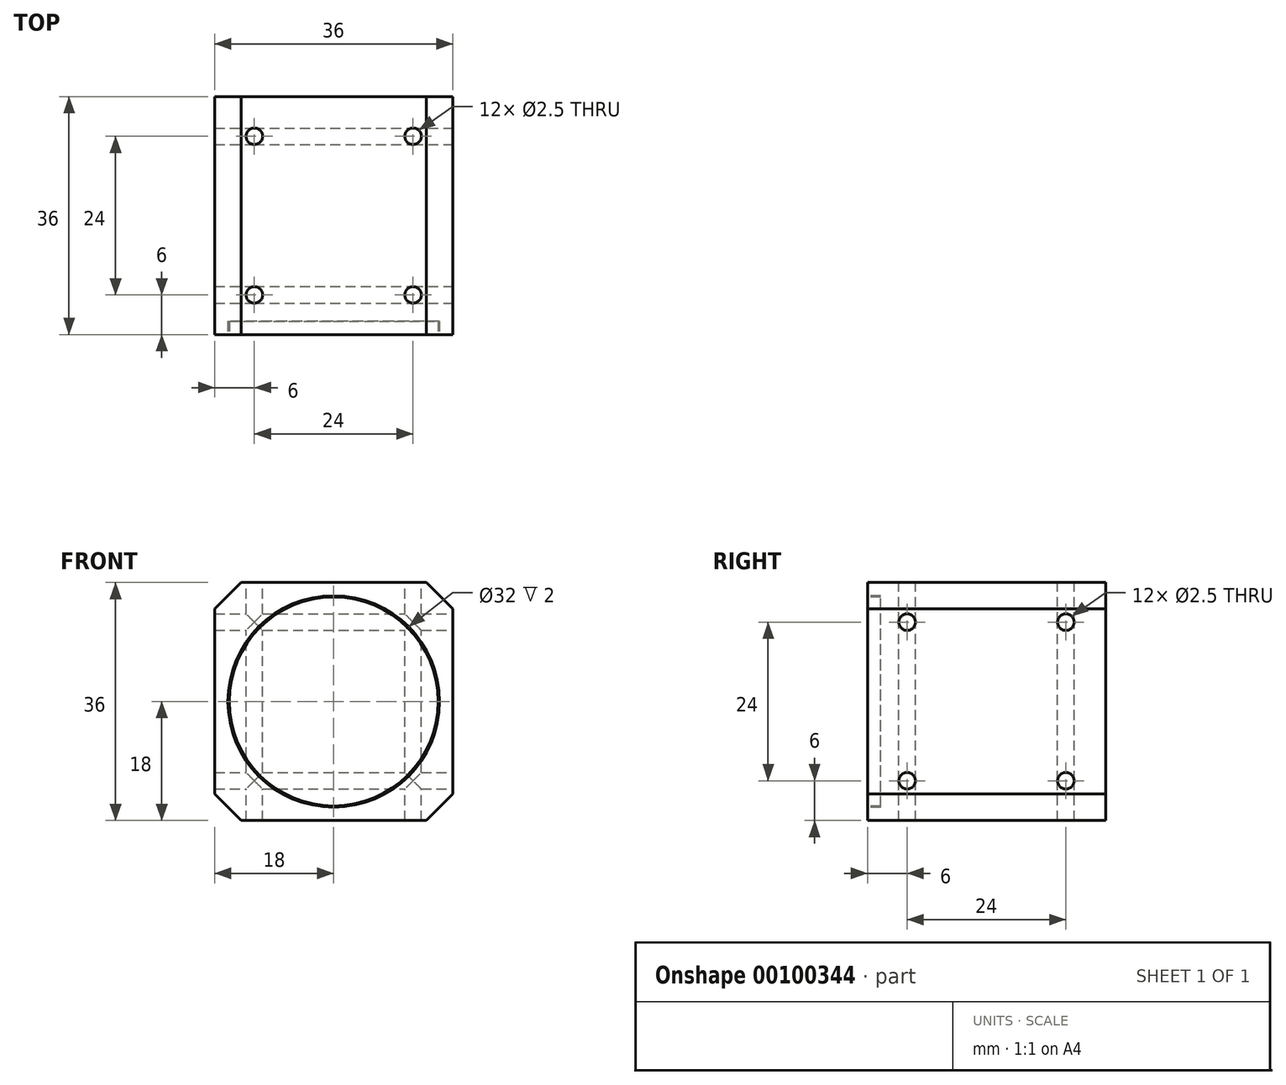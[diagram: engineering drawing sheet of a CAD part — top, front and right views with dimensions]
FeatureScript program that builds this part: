
annotation { "Feature Type Name" : "Feature", "Feature Type Description" : "" }
export const myFeature = defineFeature(function(context is Context, id is Id, definition is map)
    precondition{}
    {
        {
            var Q0;
            Q0=qCreatedBy(makeId("Front.planeOp"),FACE);
            var sketch = newSketch(context, id + "F0", { "sketchPlane" : qUnion([Q0])});
            skLineSegment(sketch, "E0.bottom", {"start": v(18, -18) * mm, "end": v(-18, -18) * mm});
            skLineSegment(sketch, "E0.top", {"start": v(18, 18) * mm, "end": v(-18, 18) * mm});
            skLineSegment(sketch, "E0.left", {"start": v(18, -18) * mm, "end": v(18, 18) * mm});
            skLineSegment(sketch, "E0.right", {"start": v(-18, -18) * mm, "end": v(-18, 18) * mm});
            skPoint(sketch, "E0.middle", {"position": v(0, 0) * mm});
            skSolve(sketch);
        }
        {
            var Q0;
            Q0 = qSketchRegion(id + "F0", true);
            extrude(context, id + "F1", {"entities" : qUnion([Q0]), "depth" : 36 * mm});
        }
        {
            var Q0;
            Q0=makeQuery(id+"F1.opExtrude","CAP_FACE",FACE,{"disambiguationData":[OSD([sQuery(id+"F0.wireOp",EDGE,"E0.bottom"),sQuery(id+"F0.wireOp",EDGE,"E0.top"),sQuery(id+"F0.wireOp",EDGE,"E0.left"),sQuery(id+"F0.wireOp",EDGE,"E0.right")])],"isStart":false});
            var sketch = newSketch(context, id + "F2", { "sketchPlane" : qUnion([Q0])});
            skCircle(sketch, "E1", {"center": v(0, 0) * mm, "radius": 16 * mm});
            skCircle(sketch, "E2", {"center": v(0, 0) * mm, "radius": 15.8 * mm});
            skSolve(sketch);
        }
        {
            var Q0;
            Q0 = qSketchRegion(id + "F2", true);
            extrude(context, id + "F3", {"entities" : qUnion([Q0]), "operationType" : NewBodyOperationType.REMOVE, "oppositeDirection" : true, "depth" : 2 * mm});
        }
        {
            var Q0;
            Q0=makeQuery(id+"F1.opExtrude","SWEPT_FACE",FACE,{"disambiguationData":[OSD([sQuery(id+"F0.wireOp",EDGE,"E0.left")])]});
            var sketch = newSketch(context, id + "F4", { "sketchPlane" : qUnion([Q0])});
            skLineSegment(sketch, "E3.0", {"start": v(-6, -12) * mm, "end": v(-6, 12) * mm, "construction": true});
            skLineSegment(sketch, "E3.1", {"start": v(-30, -12) * mm, "end": v(-6, -12) * mm, "construction": true});
            skLineSegment(sketch, "E3.2", {"start": v(-30, 12) * mm, "end": v(-30, -12) * mm, "construction": true});
            skLineSegment(sketch, "E3.3", {"start": v(-6, 12) * mm, "end": v(-30, 12) * mm, "construction": true});
            skCircle(sketch, "E4", {"center": v(-30, 12) * mm, "radius": 1.25 * mm});
            skCircle(sketch, "E5", {"center": v(-6, 12) * mm, "radius": 1.25 * mm});
            skCircle(sketch, "E6", {"center": v(-6, -12) * mm, "radius": 1.25 * mm});
            skCircle(sketch, "E7", {"center": v(-30, -12) * mm, "radius": 1.25 * mm});
            skSolve(sketch);
        }
        {
            var Q0;
            Q0 = qSketchRegion(id + "F4", true);
            extrude(context, id + "F5", {"entities" : qUnion([Q0]), "operationType" : NewBodyOperationType.REMOVE, "endBound" : BoundingType.THROUGH_ALL, "oppositeDirection" : true, "depth" : 25 * mm});
        }
        {
            var Q0;
            Q0=makeQuery(id+"F1.opExtrude","SWEPT_FACE",FACE,{"disambiguationData":[OSD([sQuery(id+"F0.wireOp",EDGE,"E0.top")])]});
            var sketch = newSketch(context, id + "F6", { "sketchPlane" : qUnion([Q0])});
            skLineSegment(sketch, "E8.0", {"start": v(12, -6) * mm, "end": v(-12, -6) * mm, "construction": true});
            skLineSegment(sketch, "E8.1", {"start": v(12, -30) * mm, "end": v(12, -6) * mm, "construction": true});
            skLineSegment(sketch, "E8.2", {"start": v(-12, -30) * mm, "end": v(12, -30) * mm, "construction": true});
            skLineSegment(sketch, "E8.3", {"start": v(-12, -6) * mm, "end": v(-12, -30) * mm, "construction": true});
            skCircle(sketch, "E9", {"center": v(-12, -30) * mm, "radius": 1.25 * mm});
            skCircle(sketch, "E10", {"center": v(-12, -6) * mm, "radius": 1.25 * mm});
            skCircle(sketch, "E11", {"center": v(12, -6) * mm, "radius": 1.25 * mm});
            skCircle(sketch, "E12", {"center": v(12, -30) * mm, "radius": 1.25 * mm});
            skSolve(sketch);
        }
        {
            var Q0;
            Q0 = qSketchRegion(id + "F6", true);
            extrude(context, id + "F7", {"entities" : qUnion([Q0]), "operationType" : NewBodyOperationType.REMOVE, "endBound" : BoundingType.THROUGH_ALL, "oppositeDirection" : true, "depth" : 25 * mm});
        }
        {
            var Q0;
            Q0=makeQuery(id+"F1.opExtrude","SWEPT_EDGE",EDGE,{"disambiguationData":[OSD([sQuery(id+"F0.wireOp",EDGE,"E0.top"),sQuery(id+"F0.wireOp",EDGE,"E0.left")])]});
            var Q1;
            Q1=makeQuery(id+"F1.opExtrude","SWEPT_EDGE",EDGE,{"disambiguationData":[OSD([sQuery(id+"F0.wireOp",EDGE,"E0.top"),sQuery(id+"F0.wireOp",EDGE,"E0.right")])]});
            var Q2;
            Q2=makeQuery(id+"F1.opExtrude","SWEPT_EDGE",EDGE,{"disambiguationData":[OSD([sQuery(id+"F0.wireOp",EDGE,"E0.bottom"),sQuery(id+"F0.wireOp",EDGE,"E0.left")])]});
            var Q3;
            Q3=makeQuery(id+"F1.opExtrude","SWEPT_EDGE",EDGE,{"disambiguationData":[OSD([sQuery(id+"F0.wireOp",EDGE,"E0.bottom"),sQuery(id+"F0.wireOp",EDGE,"E0.right")])]});
            chamfer(context, id + "F8", {"entities" : qUnion([Q0, Q1, Q2, Q3]), "width" : 4 * mm, "tangentPropagation" : true});
        }
    });
